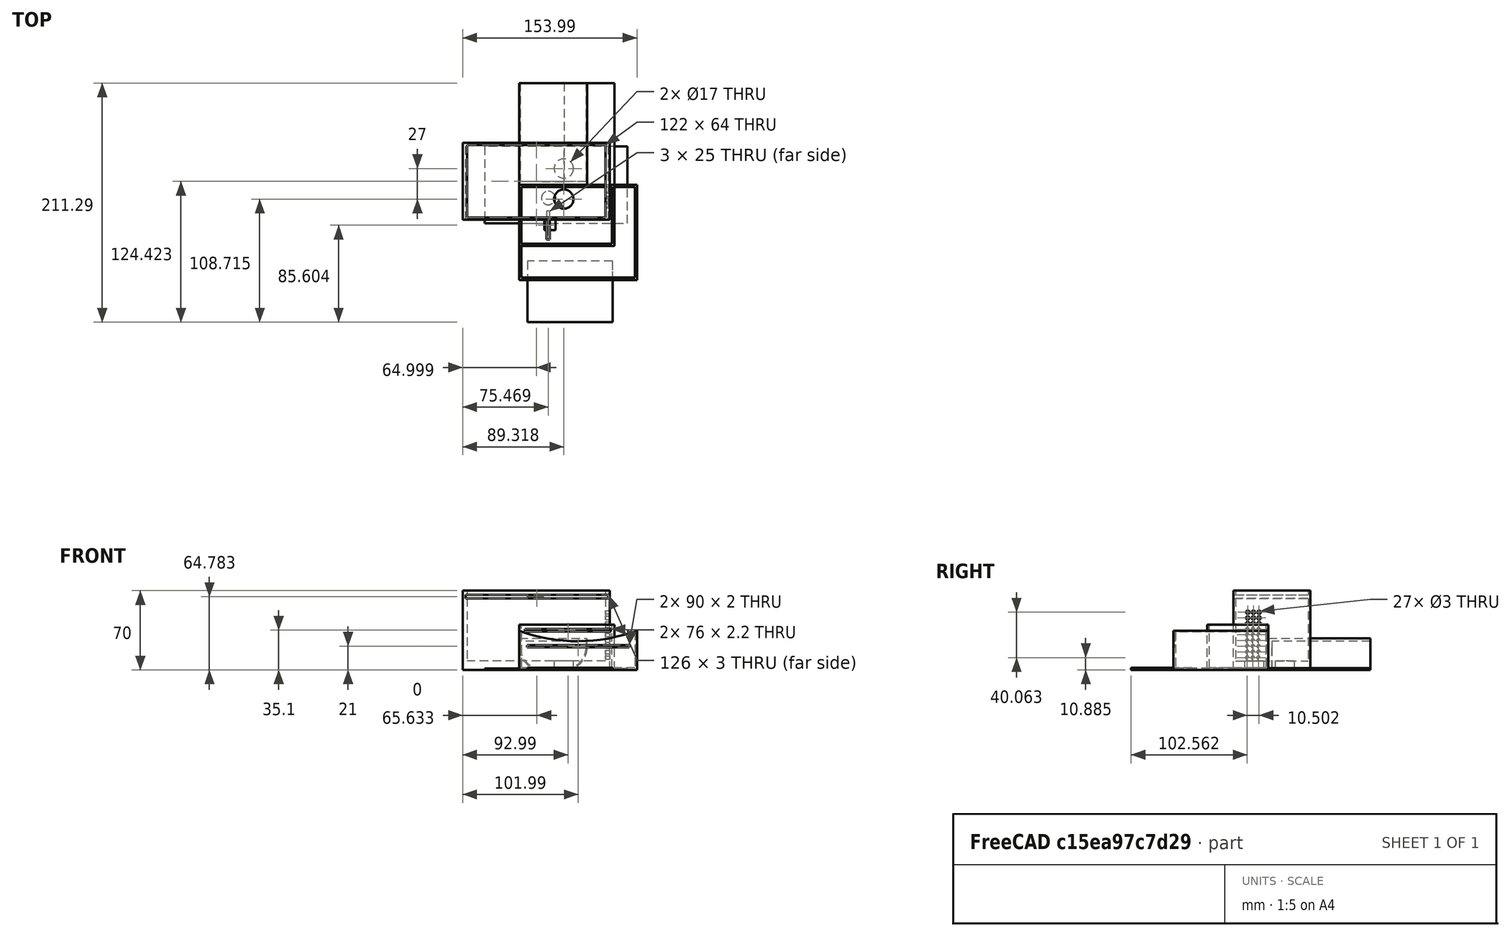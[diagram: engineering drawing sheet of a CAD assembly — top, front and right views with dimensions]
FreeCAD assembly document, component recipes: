
FREECAD ASSEMBLY — COMPONENT RECIPES ("box_snic_esp32_1")

This assembly document has 2 components, labeled P0..P1 below (a component is one placed body or linked part). 2 of them carry a construction recipe — the FreeCAD feature program that regenerates the part from scratch, quoted from this document or its linked companion documents; the rest are supplied as boundary geometry only. No exploded tour is included for this assembly.
COMPONENT P0 — recipe-attached ("Body002", modeled in this document).
Construction recipe (the document's own serialized feature program — sketch geometry with constraints, then the solid features built on it; lengths are millimeters unless a unit is written):

FEATURE [Sketcher::SketchObject] Sketch
  ArcFitTolerance = 1e-06
  AttachmentSupport = -> [Origin]
  ExternalTypes = [0]
  FullyConstrained = false
  MakeInternals = false
  MapMode = 5
  sketch-geometry (4):
    g0: LineSegment StartX=-49.9915 StartY=37.133 StartZ=0 EndX=-49.9915 EndY=-30.867 EndZ=0
    g1: LineSegment StartX=-49.9915 StartY=-30.867 StartZ=0 EndX=80.0085 EndY=-30.867 EndZ=0
    g2: LineSegment StartX=80.0085 StartY=-30.867 StartZ=0 EndX=80.0085 EndY=37.133 EndZ=0
    g3: LineSegment StartX=80.0085 StartY=37.133 StartZ=0 EndX=-49.9915 EndY=37.133 EndZ=0
  constraints (10):
    c: Coincident(g0,g1)
    c: Coincident(g1,g2)
    c: Coincident(g2,g3)
    c: Coincident(g3,g0)
    c: Vertical(g0)
    c: Vertical(g2)
    c: Horizontal(g1)
    c: Horizontal(g3)
    c: DistanceY(g2,g2) = 68
    c: DistanceX(g3,g3) = 130
FEATURE [PartDesign::Pad] Pad
  Direction = (0,0,1)
  Length = 70
  Length2 = 10
  Profile = -> Sketch
  ReferenceAxis = -> Sketch [N_Axis]
  Refine = true
  SideType = 0
  Suppressed = false
  Type = 0
  Type2 = 0
FEATURE [Sketcher::SketchObject] Sketch001
  ArcFitTolerance = 1e-06
  AttachmentSupport = -> [Pad]
  ExternalTypes = [0]
  FullyConstrained = false
  MakeInternals = false
  MapMode = 5
  Placement = pos=(0,0,70) rot=(0,0,1;0rad)
  sketch-geometry (4):
    g0: LineSegment StartX=-45.9915 StartY=35.133 StartZ=0 EndX=-45.9915 EndY=-28.867 EndZ=0
    g1: LineSegment StartX=-45.9915 StartY=-28.867 StartZ=0 EndX=76.0085 EndY=-28.867 EndZ=0
    g2: LineSegment StartX=76.0085 StartY=-28.867 StartZ=0 EndX=76.0085 EndY=35.133 EndZ=0
    g3: LineSegment StartX=76.0085 StartY=35.133 StartZ=0 EndX=-45.9915 EndY=35.133 EndZ=0
  constraints (10):
    c: Coincident(g0,g1)
    c: Coincident(g1,g2)
    c: Coincident(g2,g3)
    c: Coincident(g3,g0)
    c: Vertical(g0)
    c: Vertical(g2)
    c: Horizontal(g1)
    c: Horizontal(g3)
    c: DistanceX(g3,g3) = 122
    c: DistanceY(g0,g0) = 64
FEATURE [PartDesign::Pocket] Pocket
  BaseFeature = -> Pad
  Direction = (0,0,-1)
  Length = 62
  Length2 = 5
  Profile = -> Sketch001
  ReferenceAxis = -> Sketch001 [N_Axis]
  Refine = true
  SideType = 0
  Suppressed = false
  Type = 0
  Type2 = 0
FEATURE [Sketcher::SketchObject] Sketch002
  ArcFitTolerance = 1e-06
  AttachmentSupport = -> [Pocket]
  ExternalTypes = [0]
  FullyConstrained = false
  MakeInternals = false
  MapMode = 5
  Placement = pos=(0,-30.867,0) rot=(1,0,0;1.5708rad)
  sketch-geometry (4):
    g0: LineSegment StartX=-47.3565 StartY=66.2828 StartZ=0 EndX=-47.3565 EndY=63.2828 EndZ=0
    g1: LineSegment StartX=-47.3565 StartY=63.2828 StartZ=0 EndX=78.6435 EndY=63.2828 EndZ=0
    g2: LineSegment StartX=78.6435 StartY=63.2828 StartZ=0 EndX=78.6435 EndY=66.2828 EndZ=0
    g3: LineSegment StartX=78.6435 StartY=66.2828 StartZ=0 EndX=-47.3565 EndY=66.2828 EndZ=0
  constraints (10):
    c: Coincident(g0,g1)
    c: Coincident(g1,g2)
    c: Coincident(g2,g3)
    c: Coincident(g3,g0)
    c: Vertical(g0)
    c: Vertical(g2)
    c: Horizontal(g1)
    c: Horizontal(g3)
    c: Distance(g2,g2) = 3
    c: DistanceX(g3,g3) = 126
FEATURE [PartDesign::Pocket] Pocket001
  BaseFeature = -> Pocket
  Direction = (0,1,-2e-16)
  Length = 5
  Length2 = 5
  Profile = -> Sketch002
  ReferenceAxis = -> Sketch002 [N_Axis]
  Refine = true
  SideType = 0
  Suppressed = false
  Type = 1
  Type2 = 0
FEATURE [Sketcher::SketchObject] Sketch004
  ArcFitTolerance = 1e-06
  AttachmentSupport = -> [Pocket001]
  ExternalTypes = [0]
  FullyConstrained = false
  MakeInternals = false
  MapMode = 5
  Placement = pos=(80.0085,0,0) rot=(0.57735,0.57735,0.57735;2.0944rad)
  sketch-geometry (27):
    g0: Circle CenterX=-18.6463 CenterY=35.9546 CenterZ=0 NormalX=0 NormalY=0 NormalZ=1 AngleXU=0 Radius=1.5
    g1: Circle CenterX=-13.6463 CenterY=35.9546 CenterZ=0 NormalX=0 NormalY=0 NormalZ=1 AngleXU=0 Radius=1.5
    g2: Circle CenterX=-8.64635 CenterY=35.9546 CenterZ=0 NormalX=0 NormalY=0 NormalZ=1 AngleXU=0 Radius=1.5
    g3: Circle CenterX=-18.6874 CenterY=30.9548 CenterZ=0 NormalX=0 NormalY=0 NormalZ=1 AngleXU=0 Radius=1.5
    g4: Circle CenterX=-13.6874 CenterY=30.9548 CenterZ=0 NormalX=0 NormalY=0 NormalZ=1 AngleXU=0 Radius=1.5
    g5: Circle CenterX=-8.68742 CenterY=30.9548 CenterZ=0 NormalX=0 NormalY=0 NormalZ=1 AngleXU=0 Radius=1.5
    g6: Circle CenterX=-18.7285 CenterY=25.9549 CenterZ=0 NormalX=0 NormalY=0 NormalZ=1 AngleXU=0 Radius=1.5
    g7: Circle CenterX=-13.7285 CenterY=25.9549 CenterZ=0 NormalX=0 NormalY=0 NormalZ=1 AngleXU=0 Radius=1.5
    g8: Circle CenterX=-8.72848 CenterY=25.9549 CenterZ=0 NormalX=0 NormalY=0 NormalZ=1 AngleXU=0 Radius=1.5
    g9: Circle CenterX=-18.6463 CenterY=20.885 CenterZ=0 NormalX=0 NormalY=0 NormalZ=1 AngleXU=0 Radius=1.5
    g10: Circle CenterX=-13.6463 CenterY=20.885 CenterZ=0 NormalX=0 NormalY=0 NormalZ=1 AngleXU=0 Radius=1.5
    g11: Circle CenterX=-8.64635 CenterY=20.885 CenterZ=0 NormalX=0 NormalY=0 NormalZ=1 AngleXU=0 Radius=1.5
    g12: Circle CenterX=-18.6874 CenterY=15.8852 CenterZ=0 NormalX=0 NormalY=0 NormalZ=1 AngleXU=0 Radius=1.5
    g13: Circle CenterX=-13.6874 CenterY=15.8852 CenterZ=0 NormalX=0 NormalY=0 NormalZ=1 AngleXU=0 Radius=1.5
    g14: Circle CenterX=-8.68742 CenterY=15.8852 CenterZ=0 NormalX=0 NormalY=0 NormalZ=1 AngleXU=0 Radius=1.5
    g15: Circle CenterX=-18.7285 CenterY=10.8854 CenterZ=0 NormalX=0 NormalY=0 NormalZ=1 AngleXU=0 Radius=1.5
    g16: Circle CenterX=-13.7285 CenterY=10.8854 CenterZ=0 NormalX=0 NormalY=0 NormalZ=1 AngleXU=0 Radius=1.5
    g17: Circle CenterX=-8.72848 CenterY=10.8854 CenterZ=0 NormalX=0 NormalY=0 NormalZ=1 AngleXU=0 Radius=1.5
    g18: Circle CenterX=-18.2265 CenterY=50.9487 CenterZ=0 NormalX=0 NormalY=0 NormalZ=1 AngleXU=0 Radius=1.5
    g19: Circle CenterX=-13.2265 CenterY=50.9487 CenterZ=0 NormalX=0 NormalY=0 NormalZ=1 AngleXU=0 Radius=1.5
    g20: Circle CenterX=-8.22651 CenterY=50.9487 CenterZ=0 NormalX=0 NormalY=0 NormalZ=1 AngleXU=0 Radius=1.5
    g21: Circle CenterX=-18.2676 CenterY=45.9489 CenterZ=0 NormalX=0 NormalY=0 NormalZ=1 AngleXU=0 Radius=1.5
    g22: Circle CenterX=-13.2676 CenterY=45.9489 CenterZ=0 NormalX=0 NormalY=0 NormalZ=1 AngleXU=0 Radius=1.5
    g23: Circle CenterX=-8.26758 CenterY=45.9489 CenterZ=0 NormalX=0 NormalY=0 NormalZ=1 AngleXU=0 Radius=1.5
    g24: Circle CenterX=-18.3086 CenterY=40.9491 CenterZ=0 NormalX=0 NormalY=0 NormalZ=1 AngleXU=0 Radius=1.5
    g25: Circle CenterX=-13.3086 CenterY=40.9491 CenterZ=0 NormalX=0 NormalY=0 NormalZ=1 AngleXU=0 Radius=1.5
    g26: Circle CenterX=-8.30865 CenterY=40.9491 CenterZ=0 NormalX=0 NormalY=0 NormalZ=1 AngleXU=0 Radius=1.5
  constraints (27):
    c: Diameter(g0) = 3
    c: Diameter(g1) = 3
    c: Diameter(g2) = 3
    c: Diameter(g3) = 3
    c: Diameter(g6) = 3
    c: Diameter(g9) = 3
    c: Diameter(g12) = 3
    c: Diameter(g15) = 3
    c: Diameter(g4) = 3
    c: Diameter(g7) = 3
    c: Diameter(g10) = 3
    c: Diameter(g13) = 3
    c: Diameter(g16) = 3
    c: Diameter(g5) = 3
    c: Diameter(g8) = 3
    c: Diameter(g11) = 3
    c: Diameter(g14) = 3
    c: Diameter(g17) = 3
    c: Diameter(g18) = 3
    c: Diameter(g19) = 3
    c: Diameter(g20) = 3
    c: Diameter(g21) = 3
    c: Diameter(g24) = 3
    c: Diameter(g22) = 3
    c: Diameter(g25) = 3
    c: Diameter(g23) = 3
    c: Diameter(g26) = 3
FEATURE [PartDesign::Pocket] Pocket002
  BaseFeature = -> Pocket001
  Direction = (-1,0,0)
  Length = 5
  Length2 = 5
  Profile = -> Sketch004
  ReferenceAxis = -> Sketch004 [N_Axis]
  Refine = true
  SideType = 0
  Suppressed = false
  Type = 0
  Type2 = 0
FEATURE [Sketcher::SketchObject] Sketch005
  ArcFitTolerance = 1e-06
  AttachmentSupport = -> [Pocket002]
  ExternalTypes = [0]
  FullyConstrained = false
  MakeInternals = false
  MapMode = 5
  Placement = pos=(0,0,0) rot=(1,0,0;3.14159rad)
  sketch-geometry (2):
    g0: Circle CenterX=39.3276 CenterY=12.575 CenterZ=0 NormalX=0 NormalY=0 NormalZ=1 AngleXU=0 Radius=8.5
    g1: Circle CenterX=39.3276 CenterY=-14.425 CenterZ=0 NormalX=0 NormalY=0 NormalZ=1 AngleXU=0 Radius=8.5
  constraints (3):
    c: Diameter(g0) = 17
    c: Diameter(g1) = 17
    c: Distance(g0,g1) = 10
FEATURE [PartDesign::Pocket] Pocket003
  BaseFeature = -> Pocket002
  Direction = (0,0,1)
  Length = 5
  Length2 = 5
  Profile = -> Sketch005
  ReferenceAxis = -> Sketch005 [N_Axis]
  Refine = true
  SideType = 0
  Suppressed = false
  Type = 1
  Type2 = 0
FEATURE [PartDesign::Body] Body  label="box_1"
  AllowCompound = true
  Group = -> [Sketch,Pad,Sketch001,Pocket,Sketch002,Pocket001,Sketch004,Pocket002,Sketch005,Pocket003]
  Origin = -> Origin
  Tip = -> Pocket003
COMPONENT P1 — recipe-attached ("Body003", modeled in this document).
Construction recipe (the document's own serialized feature program — sketch geometry with constraints, then the solid features built on it; lengths are millimeters unless a unit is written):

FEATURE [Sketcher::SketchObject] Sketch003
  ArcFitTolerance = 1e-06
  AttachmentSupport = -> [Origin002]
  ExternalTypes = [0]
  FullyConstrained = false
  MakeInternals = false
  MapMode = 5
  sketch-geometry (4):
    g0: LineSegment StartX=-30.421 StartY=34 StartZ=0 EndX=-30.421 EndY=-34 EndZ=0
    g1: LineSegment StartX=-30.421 StartY=-34 StartZ=0 EndX=95.579 EndY=-34 EndZ=0
    g2: LineSegment StartX=95.579 StartY=-34 StartZ=0 EndX=95.579 EndY=34 EndZ=0
    g3: LineSegment StartX=95.579 StartY=34 StartZ=0 EndX=-30.421 EndY=34 EndZ=0
  constraints (10):
    c: Coincident(g0,g1)
    c: Coincident(g1,g2)
    c: Coincident(g2,g3)
    c: Coincident(g3,g0)
    c: Vertical(g2)
    c: Horizontal(g1)
    c: Horizontal(g3)
    c: DistanceX(g3,g3) = 126
    c: DistanceY(g2,g2) = 68
    c: Symmetric(g0,g0,g-1)
FEATURE [PartDesign::Pad] Pad001
  Direction = (0,0,1)
  Length = 1.2
  Length2 = 10
  Profile = -> Sketch003
  ReferenceAxis = -> Sketch003 [N_Axis]
  Refine = true
  SideType = 0
  Suppressed = false
  Type = 0
  Type2 = 0
FEATURE [PartDesign::Body] Body001  label="box_cover_1"
  AllowCompound = true
  Group = -> [Sketch003,Pad001]
  Origin = -> Origin002
  Tip = -> Pad001
PROVENANCE & LICENSES
A FreeCAD (.FCStd) document from a public repository crawl; recipes are the document's own serialized feature recipes (and, for linked parts, companion documents' recipes).
License: gpl-3.0.
